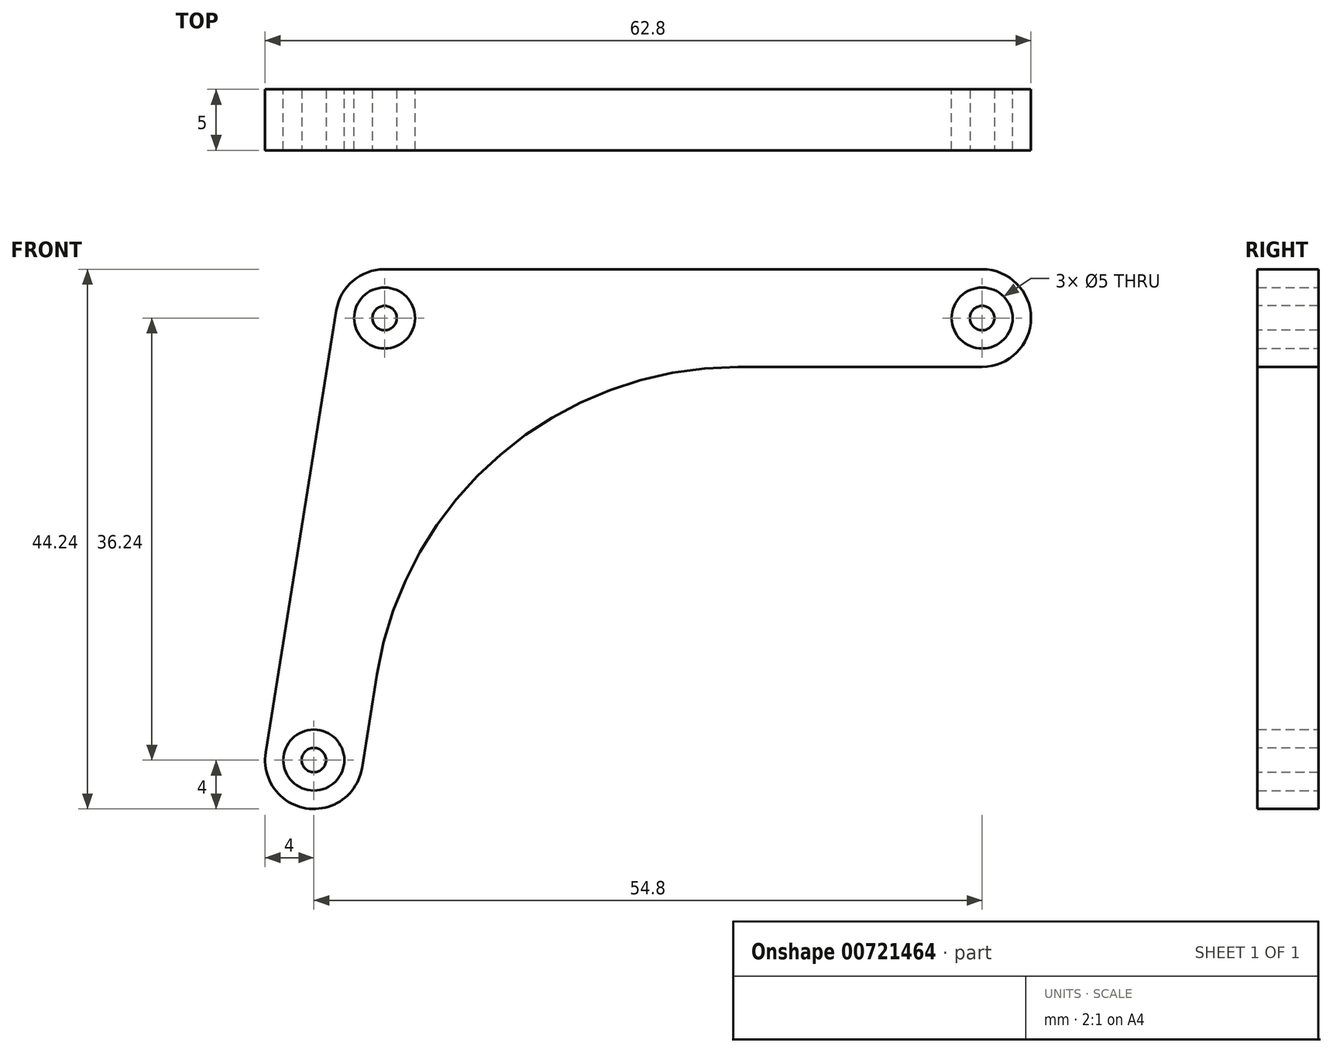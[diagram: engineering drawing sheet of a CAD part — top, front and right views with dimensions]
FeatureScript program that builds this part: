
annotation { "Feature Type Name" : "Feature", "Feature Type Description" : "" }
export const myFeature = defineFeature(function(context is Context, id is Id, definition is map)
    precondition{}
    {
        {
            var Q0;
            Q0=qCreatedBy(makeId("Front.planeOp"),FACE);
            var sketch = newSketch(context, id + "F0", { "sketchPlane" : qUnion([Q0])});
            skArc(sketch, "E0", {"start": v(0, 4) * mm, "mid": v(-2.6, 3.04) * mm, "end": v(-3.95, 0.63) * mm});
            skLineSegment(sketch, "E1.bottom", {"start": v(0, 4) * mm, "end": v(49, 4) * mm});
            skLineSegment(sketch, "E1.top", {"start": v(3.41, -4) * mm, "end": v(49, -4) * mm});
            skLineSegment(sketch, "E2", {"start": v(-3.95, 0.63) * mm, "end": v(-9.75, -35.6) * mm});
            skPoint(sketch, "E3.visualSharp", {"position": v(140.32, 902.04) * mm});
            skArc(sketch, "E3.filletArc", {"start": v(-9.75, -35.6) * mm, "mid": v(-6.43, -40.19) * mm, "end": v(-1.85, -36.87) * mm});
            skCircle(sketch, "E4", {"center": v(0, 0) * mm, "radius": 2.5 * mm});
            skArc(sketch, "E5", {"start": v(49, -4) * mm, "mid": v(53, 0) * mm, "end": v(49, 4) * mm});
            skLineSegment(sketch, "E6", {"start": v(-1.85, -36.87) * mm, "end": v(3.41, -4) * mm});
            skArc(sketch, "E7", {"start": v(29, -4) * mm, "mid": v(9.53, -11.17) * mm, "end": v(-0.63, -29.26) * mm});
            skCircle(sketch, "E8", {"center": v(49, 0) * mm, "radius": 2.5 * mm});
            skCircle(sketch, "E9", {"center": v(-5.8, -36.24) * mm, "radius": 2.5 * mm});
            skSolve(sketch);
        }
        {
            var Q0;
            Q0 = qSketchRegion(id + "F0", true);
            extrude(context, id + "F1", {"entities" : qUnion([Q0]), "endBound" : BoundingType.SYMMETRIC, "depth" : 5 * mm, "offsetDistance" : 25.4 * mm});
        }
        {
            var Q0;
            Q0=makeQuery(id+"F1.opExtrude","CAP_FACE",FACE,{"disambiguationData":[OSD([sQuery(id+"F0.wireOp",EDGE,"E0"),sQuery(id+"F0.wireOp",EDGE,"E1.bottom"),sQuery(id+"F0.wireOp",EDGE,"E1.top"),sQuery(id+"F0.wireOp",EDGE,"E2"),sQuery(id+"F0.wireOp",EDGE,"E3.filletArc"),sQuery(id+"F0.wireOp",EDGE,"E4"),sQuery(id+"F0.wireOp",EDGE,"E5"),sQuery(id+"F0.wireOp",EDGE,"E6"),sQuery(id+"F0.wireOp",EDGE,"E7"),sQuery(id+"F0.wireOp",EDGE,"E8"),sQuery(id+"F0.wireOp",EDGE,"E9")])],"isStart":false});
            var sketch = newSketch(context, id + "F2", { "sketchPlane" : qUnion([Q0])});
            skCircle(sketch, "E10", {"center": v(0, 0) * mm, "radius": 1 * mm});
            skCircle(sketch, "E11", {"center": v(-5.8, -36.24) * mm, "radius": 1 * mm});
            skCircle(sketch, "E12", {"center": v(49, 0) * mm, "radius": 1 * mm});
            skSolve(sketch);
        }
        {
            var Q0;
            Q0 = qSketchRegion(id + "F2", true);
            extrude(context, id + "F3", {"entities" : qUnion([Q0]), "oppositeDirection" : true, "depth" : 5 * mm, "offsetDistance" : 25.4 * mm});
        }
    });
